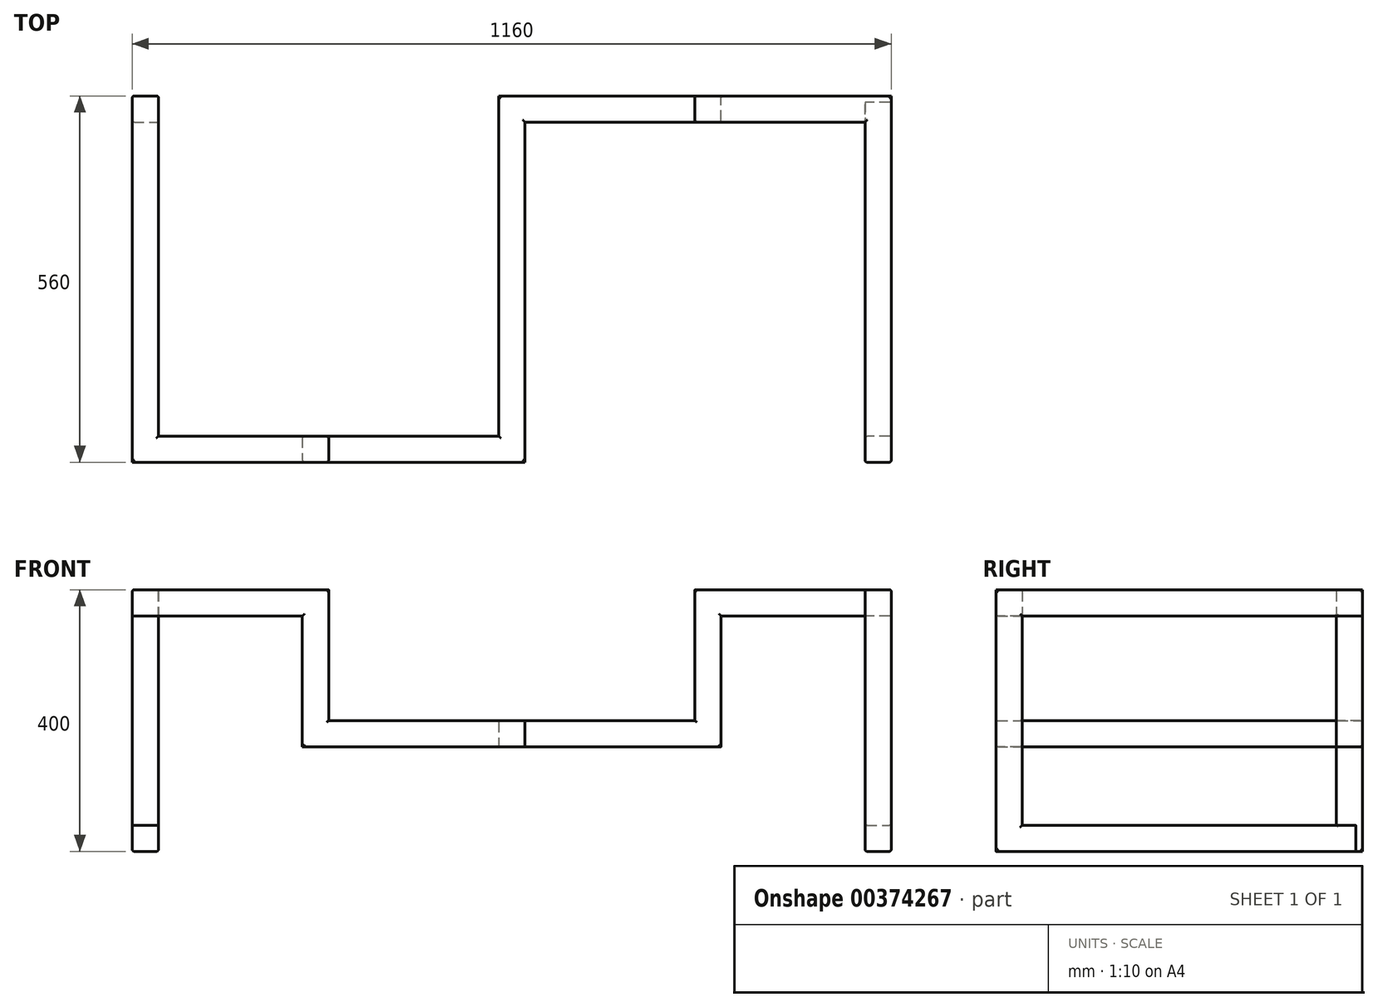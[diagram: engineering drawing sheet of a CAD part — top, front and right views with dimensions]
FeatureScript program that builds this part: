
annotation { "Feature Type Name" : "Feature", "Feature Type Description" : "" }
export const myFeature = defineFeature(function(context is Context, id is Id, definition is map)
    precondition{}
    {
        {
            var Q0;
            Q0=qCreatedBy(makeId("Front.planeOp"),FACE);
            var sketch = newSketch(context, id + "F0", { "sketchPlane" : qUnion([Q0])});
            skLineSegment(sketch, "E0.bottom", {"start": v(0, 0) * mm, "end": v(40, 0) * mm});
            skLineSegment(sketch, "E0.top", {"start": v(0, 40) * mm, "end": v(40, 40) * mm});
            skLineSegment(sketch, "E0.left", {"start": v(0, 0) * mm, "end": v(0, 40) * mm});
            skLineSegment(sketch, "E0.right", {"start": v(40, 0) * mm, "end": v(40, 40) * mm});
            skSolve(sketch);
        }
        {
            var Q0;
            Q0=makeQuery(id+"F0.imprint","IMPRINT",FACE,{"disambiguationData":[TD([[makeQuery(id+"F0.imprint","IMPRINT",EDGE,{"derivedFrom":sQuery(id+"F0.wireOp",EDGE,"E0.bottom")}),1.0]])]});
            extrude(context, id + "F1", {"entities" : qUnion([Q0]), "oppositeDirection" : true, "depth" : 560 * mm});
        }
        {
            var Q0;
            Q0=makeQuery(id+"F1.opExtrude","SWEPT_FACE",FACE,{"disambiguationData":[OSD([sQuery(id+"F0.wireOp",EDGE,"E0.top")])]});
            var sketch = newSketch(context, id + "F2", { "sketchPlane" : qUnion([Q0])});
            skLineSegment(sketch, "E1.bottom", {"start": v(0, 560) * mm, "end": v(40, 560) * mm});
            skLineSegment(sketch, "E1.top", {"start": v(0, 520) * mm, "end": v(40, 520) * mm});
            skLineSegment(sketch, "E1.left", {"start": v(0, 560) * mm, "end": v(0, 520) * mm});
            skLineSegment(sketch, "E1.right", {"start": v(40, 560) * mm, "end": v(40, 520) * mm});
            skSolve(sketch);
        }
        {
            var Q0;
            Q0=makeQuery(id+"F2.imprint","IMPRINT",FACE,{"disambiguationData":[TD([[makeQuery(id+"F2.imprint","IMPRINT",EDGE,{"derivedFrom":sQuery(id+"F2.wireOp",EDGE,"E1.bottom")}),-1.0]])]});
            extrude(context, id + "F3", {"entities" : qUnion([Q0]), "operationType" : NewBodyOperationType.ADD, "depth" : 360 * mm});
        }
        {
            var Q0;
            Q0=makeQuery(id+"F3.opExtrude","SWEPT_FACE",FACE,{"disambiguationData":[OSD([sQuery(id+"F2.wireOp",EDGE,"E1.top")])]});
            var sketch = newSketch(context, id + "F4", { "sketchPlane" : qUnion([Q0])});
            skLineSegment(sketch, "E2.bottom", {"start": v(0, 400) * mm, "end": v(40, 400) * mm});
            skLineSegment(sketch, "E2.top", {"start": v(0, 360) * mm, "end": v(40, 360) * mm});
            skLineSegment(sketch, "E2.left", {"start": v(0, 400) * mm, "end": v(0, 360) * mm});
            skLineSegment(sketch, "E2.right", {"start": v(40, 400) * mm, "end": v(40, 360) * mm});
            skSolve(sketch);
        }
        {
            var Q0;
            Q0=makeQuery(id+"F4.imprint","IMPRINT",FACE,{"disambiguationData":[TD([[makeQuery(id+"F4.imprint","IMPRINT",EDGE,{"derivedFrom":sQuery(id+"F4.wireOp",EDGE,"E2.bottom")}),-1.0]])]});
            extrude(context, id + "F5", {"entities" : qUnion([Q0]), "operationType" : NewBodyOperationType.ADD, "depth" : 520 * mm});
        }
        {
            var Q0;
            Q0=makeQuery(id+"F5.boolean.opBoolean","MERGE",FACE,{"derivedFrom":[makeQuery(id+"F3.boolean.opBoolean","MERGE",FACE,{"derivedFrom":[makeQuery(id+"F1.opExtrude","SWEPT_FACE",FACE,{"disambiguationData":[OSD([sQuery(id+"F0.wireOp",EDGE,"E0.right")])]}),makeQuery(id+"F3.opExtrude","SWEPT_FACE",FACE,{"disambiguationData":[OSD([sQuery(id+"F2.wireOp",EDGE,"E1.right")])]})]}),makeQuery(id+"F5.opExtrude","SWEPT_FACE",FACE,{"disambiguationData":[OSD([sQuery(id+"F4.wireOp",EDGE,"E2.right")])]})]});
            var sketch = newSketch(context, id + "F6", { "sketchPlane" : qUnion([Q0])});
            skLineSegment(sketch, "E3.bottom", {"start": v(0, 400) * mm, "end": v(40, 400) * mm});
            skLineSegment(sketch, "E3.top", {"start": v(0, 360) * mm, "end": v(40, 360) * mm});
            skLineSegment(sketch, "E3.left", {"start": v(0, 400) * mm, "end": v(0, 360) * mm});
            skLineSegment(sketch, "E3.right", {"start": v(40, 400) * mm, "end": v(40, 360) * mm});
            skSolve(sketch);
        }
        {
            var Q0;
            Q0 = qSketchRegion(id + "F6", true);
            extrude(context, id + "F7", {"entities" : qUnion([Q0]), "operationType" : NewBodyOperationType.ADD, "depth" : 260 * mm});
        }
        {
            var Q0;
            Q0=makeQuery(id+"F7.boolean.opBoolean","MERGE",FACE,{"derivedFrom":[makeQuery(id+"F5.opExtrude","SWEPT_FACE",FACE,{"disambiguationData":[OSD([sQuery(id+"F4.wireOp",EDGE,"E2.top")])]}),makeQuery(id+"F7.opExtrude","SWEPT_FACE",FACE,{"disambiguationData":[OSD([sQuery(id+"F6.wireOp",EDGE,"E3.top")])]})]});
            var sketch = newSketch(context, id + "F8", { "sketchPlane" : qUnion([Q0])});
            skLineSegment(sketch, "E4.bottom", {"start": v(300, -40) * mm, "end": v(260, -40) * mm});
            skLineSegment(sketch, "E4.top", {"start": v(300, 0) * mm, "end": v(260, 0) * mm});
            skLineSegment(sketch, "E4.left", {"start": v(300, -40) * mm, "end": v(300, 0) * mm});
            skLineSegment(sketch, "E4.right", {"start": v(260, -40) * mm, "end": v(260, 0) * mm});
            skSolve(sketch);
        }
        {
            var Q0;
            Q0 = qSketchRegion(id + "F8", true);
            extrude(context, id + "F9", {"entities" : qUnion([Q0]), "operationType" : NewBodyOperationType.ADD, "depth" : 200 * mm});
        }
        {
            var Q0;
            Q0=makeQuery(id+"F9.boolean.opBoolean","MERGE",FACE,{"derivedFrom":[makeQuery(id+"F7.opExtrude","CAP_FACE",FACE,{"disambiguationData":[OSD([sQuery(id+"F6.wireOp",EDGE,"E3.bottom"),sQuery(id+"F6.wireOp",EDGE,"E3.top"),sQuery(id+"F6.wireOp",EDGE,"E3.left"),sQuery(id+"F6.wireOp",EDGE,"E3.right")])],"isStart":false}),makeQuery(id+"F9.opExtrude","SWEPT_FACE",FACE,{"disambiguationData":[OSD([sQuery(id+"F8.wireOp",EDGE,"E4.left")])]})]});
            var sketch = newSketch(context, id + "F10", { "sketchPlane" : qUnion([Q0])});
            skLineSegment(sketch, "E5.bottom", {"start": v(0, 160) * mm, "end": v(40, 160) * mm});
            skLineSegment(sketch, "E5.top", {"start": v(0, 200) * mm, "end": v(40, 200) * mm});
            skLineSegment(sketch, "E5.left", {"start": v(0, 160) * mm, "end": v(0, 200) * mm});
            skLineSegment(sketch, "E5.right", {"start": v(40, 160) * mm, "end": v(40, 200) * mm});
            skSolve(sketch);
        }
        {
            var Q0;
            Q0 = qSketchRegion(id + "F10", true);
            extrude(context, id + "F11", {"entities" : qUnion([Q0]), "operationType" : NewBodyOperationType.ADD, "depth" : 300 * mm});
        }
        {
            var Q0;
            Q0=makeQuery(id+"F11.boolean.opBoolean","MERGE",FACE,{"derivedFrom":[makeQuery(id+"F9.boolean.opBoolean","MERGE",FACE,{"derivedFrom":[makeQuery(id+"F7.opExtrude","SWEPT_FACE",FACE,{"disambiguationData":[OSD([sQuery(id+"F6.wireOp",EDGE,"E3.right")])]}),makeQuery(id+"F9.opExtrude","SWEPT_FACE",FACE,{"disambiguationData":[OSD([sQuery(id+"F8.wireOp",EDGE,"E4.bottom")])]})]}),makeQuery(id+"F11.opExtrude","SWEPT_FACE",FACE,{"disambiguationData":[OSD([sQuery(id+"F10.wireOp",EDGE,"E5.right")])]})]});
            var sketch = newSketch(context, id + "F12", { "sketchPlane" : qUnion([Q0])});
            skLineSegment(sketch, "E6.bottom", {"start": v(-600, 200) * mm, "end": v(-560, 200) * mm});
            skLineSegment(sketch, "E6.top", {"start": v(-600, 160) * mm, "end": v(-560, 160) * mm});
            skLineSegment(sketch, "E6.left", {"start": v(-600, 200) * mm, "end": v(-600, 160) * mm});
            skLineSegment(sketch, "E6.right", {"start": v(-560, 200) * mm, "end": v(-560, 160) * mm});
            skSolve(sketch);
        }
        {
            var Q0;
            Q0 = qSketchRegion(id + "F12", true);
            extrude(context, id + "F13", {"entities" : qUnion([Q0]), "operationType" : NewBodyOperationType.ADD, "depth" : 520 * mm});
        }
        {
            var Q0;
            Q0=makeQuery(id+"F13.boolean.opBoolean","MERGE",FACE,{"derivedFrom":[makeQuery(id+"F11.opExtrude","CAP_FACE",FACE,{"disambiguationData":[OSD([sQuery(id+"F10.wireOp",EDGE,"E5.bottom"),sQuery(id+"F10.wireOp",EDGE,"E5.top"),sQuery(id+"F10.wireOp",EDGE,"E5.left"),sQuery(id+"F10.wireOp",EDGE,"E5.right")])],"isStart":false}),makeQuery(id+"F13.opExtrude","SWEPT_FACE",FACE,{"disambiguationData":[OSD([sQuery(id+"F12.wireOp",EDGE,"E6.left")])]})]});
            var sketch = newSketch(context, id + "F14", { "sketchPlane" : qUnion([Q0])});
            skLineSegment(sketch, "E7.bottom", {"start": v(560, 200) * mm, "end": v(520, 200) * mm});
            skLineSegment(sketch, "E7.top", {"start": v(560, 160) * mm, "end": v(520, 160) * mm});
            skLineSegment(sketch, "E7.left", {"start": v(560, 200) * mm, "end": v(560, 160) * mm});
            skLineSegment(sketch, "E7.right", {"start": v(520, 200) * mm, "end": v(520, 160) * mm});
            skSolve(sketch);
        }
        {
            var Q0;
            Q0 = qSketchRegion(id + "F14", true);
            extrude(context, id + "F15", {"entities" : qUnion([Q0]), "operationType" : NewBodyOperationType.ADD, "depth" : 300 * mm});
        }
        {
            var Q0;
            Q0=makeQuery(id+"F15.boolean.opBoolean","MERGE",FACE,{"derivedFrom":[makeQuery(id+"F13.boolean.opBoolean","MERGE",FACE,{"derivedFrom":[makeQuery(id+"F11.opExtrude","SWEPT_FACE",FACE,{"disambiguationData":[OSD([sQuery(id+"F10.wireOp",EDGE,"E5.top")])]}),makeQuery(id+"F13.opExtrude","SWEPT_FACE",FACE,{"disambiguationData":[OSD([sQuery(id+"F12.wireOp",EDGE,"E6.bottom")])]})]}),makeQuery(id+"F15.opExtrude","SWEPT_FACE",FACE,{"disambiguationData":[OSD([sQuery(id+"F14.wireOp",EDGE,"E7.bottom")])]})]});
            var sketch = newSketch(context, id + "F16", { "sketchPlane" : qUnion([Q0])});
            skLineSegment(sketch, "E8.bottom", {"start": v(900, 520) * mm, "end": v(860, 520) * mm});
            skLineSegment(sketch, "E8.top", {"start": v(900, 560) * mm, "end": v(860, 560) * mm});
            skLineSegment(sketch, "E8.left", {"start": v(900, 520) * mm, "end": v(900, 560) * mm});
            skLineSegment(sketch, "E8.right", {"start": v(860, 520) * mm, "end": v(860, 560) * mm});
            skSolve(sketch);
        }
        {
            var Q0;
            Q0 = qSketchRegion(id + "F16", true);
            extrude(context, id + "F17", {"entities" : qUnion([Q0]), "operationType" : NewBodyOperationType.ADD, "depth" : 200 * mm});
        }
        {
            var Q0;
            Q0=makeQuery(id+"F17.boolean.opBoolean","MERGE",FACE,{"derivedFrom":[makeQuery(id+"F15.opExtrude","CAP_FACE",FACE,{"disambiguationData":[OSD([sQuery(id+"F14.wireOp",EDGE,"E7.bottom"),sQuery(id+"F14.wireOp",EDGE,"E7.top"),sQuery(id+"F14.wireOp",EDGE,"E7.left"),sQuery(id+"F14.wireOp",EDGE,"E7.right")])],"isStart":false}),makeQuery(id+"F17.opExtrude","SWEPT_FACE",FACE,{"disambiguationData":[OSD([sQuery(id+"F16.wireOp",EDGE,"E8.left")])]})]});
            var sketch = newSketch(context, id + "F18", { "sketchPlane" : qUnion([Q0])});
            skLineSegment(sketch, "E9.bottom", {"start": v(520, 400) * mm, "end": v(560, 400) * mm});
            skLineSegment(sketch, "E9.top", {"start": v(520, 360) * mm, "end": v(560, 360) * mm});
            skLineSegment(sketch, "E9.left", {"start": v(520, 400) * mm, "end": v(520, 360) * mm});
            skLineSegment(sketch, "E9.right", {"start": v(560, 400) * mm, "end": v(560, 360) * mm});
            skSolve(sketch);
        }
        {
            var Q0;
            Q0 = qSketchRegion(id + "F18", true);
            extrude(context, id + "F19", {"entities" : qUnion([Q0]), "operationType" : NewBodyOperationType.ADD, "depth" : 260 * mm});
        }
        {
            var Q0;
            Q0=makeQuery(id+"F19.boolean.opBoolean","MERGE",FACE,{"derivedFrom":[makeQuery(id+"F17.boolean.opBoolean","MERGE",FACE,{"derivedFrom":[makeQuery(id+"F15.opExtrude","SWEPT_FACE",FACE,{"disambiguationData":[OSD([sQuery(id+"F14.wireOp",EDGE,"E7.right")])]}),makeQuery(id+"F17.opExtrude","SWEPT_FACE",FACE,{"disambiguationData":[OSD([sQuery(id+"F16.wireOp",EDGE,"E8.bottom")])]})]}),makeQuery(id+"F19.opExtrude","SWEPT_FACE",FACE,{"disambiguationData":[OSD([sQuery(id+"F18.wireOp",EDGE,"E9.left")])]})]});
            var sketch = newSketch(context, id + "F20", { "sketchPlane" : qUnion([Q0])});
            skLineSegment(sketch, "E10.bottom", {"start": v(1160, 400) * mm, "end": v(1120, 400) * mm});
            skLineSegment(sketch, "E10.top", {"start": v(1160, 360) * mm, "end": v(1120, 360) * mm});
            skLineSegment(sketch, "E10.left", {"start": v(1160, 400) * mm, "end": v(1160, 360) * mm});
            skLineSegment(sketch, "E10.right", {"start": v(1120, 400) * mm, "end": v(1120, 360) * mm});
            skSolve(sketch);
        }
        {
            var Q0;
            Q0 = qSketchRegion(id + "F20", true);
            extrude(context, id + "F21", {"entities" : qUnion([Q0]), "operationType" : NewBodyOperationType.ADD, "depth" : 520 * mm});
        }
        {
            var Q0;
            Q0=makeQuery(id+"F21.boolean.opBoolean","MERGE",FACE,{"derivedFrom":[makeQuery(id+"F19.opExtrude","SWEPT_FACE",FACE,{"disambiguationData":[OSD([sQuery(id+"F18.wireOp",EDGE,"E9.top")])]}),makeQuery(id+"F21.opExtrude","SWEPT_FACE",FACE,{"disambiguationData":[OSD([sQuery(id+"F20.wireOp",EDGE,"E10.top")])]})]});
            var sketch = newSketch(context, id + "F22", { "sketchPlane" : qUnion([Q0])});
            skLineSegment(sketch, "E11.bottom", {"start": v(1160, 0) * mm, "end": v(1120, 0) * mm});
            skLineSegment(sketch, "E11.top", {"start": v(1160, -40) * mm, "end": v(1120, -40) * mm});
            skLineSegment(sketch, "E11.left", {"start": v(1160, 0) * mm, "end": v(1160, -40) * mm});
            skLineSegment(sketch, "E11.right", {"start": v(1120, 0) * mm, "end": v(1120, -40) * mm});
            skSolve(sketch);
        }
        {
            var Q0;
            Q0 = qSketchRegion(id + "F22", true);
            extrude(context, id + "F23", {"entities" : qUnion([Q0]), "operationType" : NewBodyOperationType.ADD, "depth" : 360 * mm});
        }
        {
            var Q0;
            Q0=makeQuery(id+"F23.opExtrude","SWEPT_FACE",FACE,{"disambiguationData":[OSD([sQuery(id+"F22.wireOp",EDGE,"E11.top")])]});
            var sketch = newSketch(context, id + "F24", { "sketchPlane" : qUnion([Q0])});
            skLineSegment(sketch, "E12.bottom", {"start": v(-1120, 0) * mm, "end": v(-1160, 0) * mm});
            skLineSegment(sketch, "E12.top", {"start": v(-1120, 40) * mm, "end": v(-1160, 40) * mm});
            skLineSegment(sketch, "E12.left", {"start": v(-1120, 0) * mm, "end": v(-1120, 40) * mm});
            skLineSegment(sketch, "E12.right", {"start": v(-1160, 0) * mm, "end": v(-1160, 40) * mm});
            skSolve(sketch);
        }
        {
            var Q0;
            Q0 = qSketchRegion(id + "F24", true);
            extrude(context, id + "F25", {"entities" : qUnion([Q0]), "operationType" : NewBodyOperationType.ADD, "depth" : 510 * mm});
        }
        {
            var Q0;
            Q0=makeQuery(id+"F5.boolean.opBoolean","MERGE",EDGE,{"derivedFrom":[makeQuery(id+"F3.opExtrude","CAP_EDGE",EDGE,{"disambiguationData":[OSD([sQuery(id+"F2.wireOp",EDGE,"E1.left")])],"isStart":false}),makeQuery(id+"F5.opExtrude","SWEPT_EDGE",EDGE,{"disambiguationData":[OSD([sQuery(id+"F4.wireOp",EDGE,"E2.bottom"),sQuery(id+"F4.wireOp",EDGE,"E2.left")])]})]});
            var Q1;
            Q1=makeQuery(id+"F7.boolean.opBoolean","MERGE",EDGE,{"derivedFrom":[makeQuery(id+"F5.opExtrude","CAP_EDGE",EDGE,{"disambiguationData":[OSD([sQuery(id+"F4.wireOp",EDGE,"E2.bottom")])],"isStart":false}),makeQuery(id+"F7.opExtrude","SWEPT_EDGE",EDGE,{"disambiguationData":[OSD([sQuery(id+"F6.wireOp",EDGE,"E3.bottom"),sQuery(id+"F6.wireOp",EDGE,"E3.left")])]})]});
            var Q2;
            Q2=makeQuery(id+"F7.opExtrude","SWEPT_EDGE",EDGE,{"disambiguationData":[OSD([sQuery(id+"F2.wireOp",EDGE,"E1.right"),sQuery(id+"F4.wireOp",EDGE,"E2.bottom"),sQuery(id+"F4.wireOp",EDGE,"E2.right"),sQuery(id+"F6.wireOp",EDGE,"E3.bottom"),sQuery(id+"F6.wireOp",EDGE,"E3.right")])]});
            var Q3;
            Q3=makeQuery(id+"F5.boolean.opBoolean","MERGE",EDGE,{"derivedFrom":[makeQuery(id+"F3.opExtrude","CAP_EDGE",EDGE,{"disambiguationData":[OSD([sQuery(id+"F2.wireOp",EDGE,"E1.right")])],"isStart":false}),makeQuery(id+"F5.opExtrude","SWEPT_EDGE",EDGE,{"disambiguationData":[OSD([sQuery(id+"F4.wireOp",EDGE,"E2.bottom"),sQuery(id+"F4.wireOp",EDGE,"E2.right")])]})]});
            var Q4;
            Q4=makeQuery(id+"F5.opExtrude","SWEPT_EDGE",EDGE,{"disambiguationData":[OSD([sQuery(id+"F0.wireOp",EDGE,"E0.top"),sQuery(id+"F0.wireOp",EDGE,"E0.left"),sQuery(id+"F2.wireOp",EDGE,"E1.top"),sQuery(id+"F2.wireOp",EDGE,"E1.left"),sQuery(id+"F4.wireOp",EDGE,"E2.top"),sQuery(id+"F4.wireOp",EDGE,"E2.left")])]});
            var Q5;
            Q5=makeQuery(id+"F7.boolean.opBoolean","MERGE",EDGE,{"derivedFrom":[makeQuery(id+"F5.opExtrude","CAP_EDGE",EDGE,{"disambiguationData":[OSD([sQuery(id+"F4.wireOp",EDGE,"E2.top")])],"isStart":false}),makeQuery(id+"F7.opExtrude","SWEPT_EDGE",EDGE,{"disambiguationData":[OSD([sQuery(id+"F6.wireOp",EDGE,"E3.top"),sQuery(id+"F6.wireOp",EDGE,"E3.left")])]})]});
            var Q6;
            Q6=makeQuery(id+"F9.opExtrude","SWEPT_EDGE",EDGE,{"disambiguationData":[OSD([sQuery(id+"F4.wireOp",EDGE,"E2.top"),sQuery(id+"F6.wireOp",EDGE,"E3.top"),sQuery(id+"F6.wireOp",EDGE,"E3.left"),sQuery(id+"F8.wireOp",EDGE,"E4.top"),sQuery(id+"F8.wireOp",EDGE,"E4.right")])]});
            var Q7;
            Q7=makeQuery(id+"F9.opExtrude","SWEPT_EDGE",EDGE,{"disambiguationData":[OSD([sQuery(id+"F0.wireOp",EDGE,"E0.top"),sQuery(id+"F0.wireOp",EDGE,"E0.right"),sQuery(id+"F2.wireOp",EDGE,"E1.top"),sQuery(id+"F2.wireOp",EDGE,"E1.right"),sQuery(id+"F4.wireOp",EDGE,"E2.top"),sQuery(id+"F4.wireOp",EDGE,"E2.right"),sQuery(id+"F6.wireOp",EDGE,"E3.top"),sQuery(id+"F6.wireOp",EDGE,"E3.right"),sQuery(id+"F8.wireOp",EDGE,"E4.bottom"),sQuery(id+"F8.wireOp",EDGE,"E4.right")])]});
            var Q8;
            Q8=makeQuery(id+"F9.boolean.opBoolean","MERGE",EDGE,{"derivedFrom":[makeQuery(id+"F7.opExtrude","CAP_EDGE",EDGE,{"disambiguationData":[OSD([sQuery(id+"F6.wireOp",EDGE,"E3.left")])],"isStart":false}),makeQuery(id+"F9.opExtrude","SWEPT_EDGE",EDGE,{"disambiguationData":[OSD([sQuery(id+"F8.wireOp",EDGE,"E4.top"),sQuery(id+"F8.wireOp",EDGE,"E4.left")])]})]});
            var Q9;
            Q9=makeQuery(id+"F11.opExtrude","SWEPT_EDGE",EDGE,{"disambiguationData":[OSD([sQuery(id+"F6.wireOp",EDGE,"E3.right"),sQuery(id+"F8.wireOp",EDGE,"E4.bottom"),sQuery(id+"F8.wireOp",EDGE,"E4.left"),sQuery(id+"F10.wireOp",EDGE,"E5.top"),sQuery(id+"F10.wireOp",EDGE,"E5.right")])]});
            var Q10;
            Q10=makeQuery(id+"F11.opExtrude","SWEPT_EDGE",EDGE,{"disambiguationData":[OSD([sQuery(id+"F6.wireOp",EDGE,"E3.left"),sQuery(id+"F8.wireOp",EDGE,"E4.top"),sQuery(id+"F8.wireOp",EDGE,"E4.left"),sQuery(id+"F10.wireOp",EDGE,"E5.top"),sQuery(id+"F10.wireOp",EDGE,"E5.left")])]});
            var Q11;
            Q11=makeQuery(id+"F11.boolean.opBoolean","MERGE",EDGE,{"derivedFrom":[makeQuery(id+"F9.opExtrude","CAP_EDGE",EDGE,{"disambiguationData":[OSD([sQuery(id+"F8.wireOp",EDGE,"E4.top")])],"isStart":false}),makeQuery(id+"F11.opExtrude","SWEPT_EDGE",EDGE,{"disambiguationData":[OSD([sQuery(id+"F10.wireOp",EDGE,"E5.bottom"),sQuery(id+"F10.wireOp",EDGE,"E5.left")])]})]});
            var Q12;
            Q12=makeQuery(id+"F3.opExtrude","SWEPT_EDGE",EDGE,{"disambiguationData":[OSD([sQuery(id+"F0.wireOp",EDGE,"E0.top"),sQuery(id+"F0.wireOp",EDGE,"E0.right"),sQuery(id+"F2.wireOp",EDGE,"E1.top"),sQuery(id+"F2.wireOp",EDGE,"E1.right")])]});
            var Q13;
            Q13=makeQuery(id+"F3.opExtrude","SWEPT_EDGE",EDGE,{"disambiguationData":[OSD([sQuery(id+"F0.wireOp",EDGE,"E0.top"),sQuery(id+"F0.wireOp",EDGE,"E0.left"),sQuery(id+"F2.wireOp",EDGE,"E1.top"),sQuery(id+"F2.wireOp",EDGE,"E1.left")])]});
            var Q14;
            Q14=makeQuery(id+"F3.boolean.opBoolean","MERGE",EDGE,{"derivedFrom":[makeQuery(id+"F1.opExtrude","CAP_EDGE",EDGE,{"disambiguationData":[OSD([sQuery(id+"F0.wireOp",EDGE,"E0.left")])],"isStart":false}),makeQuery(id+"F3.opExtrude","SWEPT_EDGE",EDGE,{"disambiguationData":[OSD([sQuery(id+"F2.wireOp",EDGE,"E1.bottom"),sQuery(id+"F2.wireOp",EDGE,"E1.left")])]})]});
            var Q15;
            Q15=makeQuery(id+"F1.opExtrude","SWEPT_EDGE",EDGE,{"disambiguationData":[OSD([sQuery(id+"F0.wireOp",EDGE,"E0.top"),sQuery(id+"F0.wireOp",EDGE,"E0.left")])]});
            var Q16;
            Q16=makeQuery(id+"F1.opExtrude","SWEPT_EDGE",EDGE,{"disambiguationData":[OSD([sQuery(id+"F0.wireOp",EDGE,"E0.bottom"),sQuery(id+"F0.wireOp",EDGE,"E0.left")])]});
            var Q17;
            Q17=makeQuery(id+"F1.opExtrude","SWEPT_EDGE",EDGE,{"disambiguationData":[OSD([sQuery(id+"F0.wireOp",EDGE,"E0.top"),sQuery(id+"F0.wireOp",EDGE,"E0.right")])]});
            var Q18;
            Q18=makeQuery(id+"F13.opExtrude","SWEPT_EDGE",EDGE,{"disambiguationData":[OSD([sQuery(id+"F6.wireOp",EDGE,"E3.right"),sQuery(id+"F8.wireOp",EDGE,"E4.bottom"),sQuery(id+"F8.wireOp",EDGE,"E4.left"),sQuery(id+"F10.wireOp",EDGE,"E5.top"),sQuery(id+"F10.wireOp",EDGE,"E5.right"),sQuery(id+"F12.wireOp",EDGE,"E6.bottom"),sQuery(id+"F12.wireOp",EDGE,"E6.right")])]});
            var Q19;
            Q19=makeQuery(id+"F13.boolean.opBoolean","MERGE",EDGE,{"derivedFrom":[makeQuery(id+"F11.opExtrude","CAP_EDGE",EDGE,{"disambiguationData":[OSD([sQuery(id+"F10.wireOp",EDGE,"E5.top")])],"isStart":false}),makeQuery(id+"F13.opExtrude","SWEPT_EDGE",EDGE,{"disambiguationData":[OSD([sQuery(id+"F12.wireOp",EDGE,"E6.bottom"),sQuery(id+"F12.wireOp",EDGE,"E6.left")])]})]});
            var Q20;
            Q20=makeQuery(id+"F15.boolean.opBoolean","MERGE",EDGE,{"derivedFrom":[makeQuery(id+"F13.opExtrude","CAP_EDGE",EDGE,{"disambiguationData":[OSD([sQuery(id+"F12.wireOp",EDGE,"E6.bottom")])],"isStart":false}),makeQuery(id+"F15.opExtrude","SWEPT_EDGE",EDGE,{"disambiguationData":[OSD([sQuery(id+"F14.wireOp",EDGE,"E7.bottom"),sQuery(id+"F14.wireOp",EDGE,"E7.left")])]})]});
            var Q21;
            Q21=makeQuery(id+"F15.opExtrude","SWEPT_EDGE",EDGE,{"disambiguationData":[OSD([sQuery(id+"F10.wireOp",EDGE,"E5.top"),sQuery(id+"F12.wireOp",EDGE,"E6.bottom"),sQuery(id+"F12.wireOp",EDGE,"E6.left"),sQuery(id+"F14.wireOp",EDGE,"E7.bottom"),sQuery(id+"F14.wireOp",EDGE,"E7.right")])]});
            var Q22;
            Q22=makeQuery(id+"F15.opExtrude","SWEPT_EDGE",EDGE,{"disambiguationData":[OSD([sQuery(id+"F10.wireOp",EDGE,"E5.bottom"),sQuery(id+"F12.wireOp",EDGE,"E6.top"),sQuery(id+"F12.wireOp",EDGE,"E6.left"),sQuery(id+"F14.wireOp",EDGE,"E7.top"),sQuery(id+"F14.wireOp",EDGE,"E7.right")])]});
            var Q23;
            Q23=makeQuery(id+"F13.opExtrude","SWEPT_EDGE",EDGE,{"disambiguationData":[OSD([sQuery(id+"F8.wireOp",EDGE,"E4.bottom"),sQuery(id+"F10.wireOp",EDGE,"E5.bottom"),sQuery(id+"F10.wireOp",EDGE,"E5.right"),sQuery(id+"F12.wireOp",EDGE,"E6.top"),sQuery(id+"F12.wireOp",EDGE,"E6.right")])]});
            var Q24;
            Q24=makeQuery(id+"F25.boolean.opBoolean","MERGE",EDGE,{"derivedFrom":[makeQuery(id+"F23.opExtrude","CAP_EDGE",EDGE,{"disambiguationData":[OSD([sQuery(id+"F22.wireOp",EDGE,"E11.right")])],"isStart":false}),makeQuery(id+"F25.opExtrude","SWEPT_EDGE",EDGE,{"disambiguationData":[OSD([sQuery(id+"F24.wireOp",EDGE,"E12.bottom"),sQuery(id+"F24.wireOp",EDGE,"E12.left")])]})]});
            var Q25;
            Q25=makeQuery(id+"F25.opExtrude","SWEPT_EDGE",EDGE,{"disambiguationData":[OSD([sQuery(id+"F18.wireOp",EDGE,"E9.top"),sQuery(id+"F20.wireOp",EDGE,"E10.top"),sQuery(id+"F20.wireOp",EDGE,"E10.left"),sQuery(id+"F22.wireOp",EDGE,"E11.top"),sQuery(id+"F22.wireOp",EDGE,"E11.left"),sQuery(id+"F24.wireOp",EDGE,"E12.top"),sQuery(id+"F24.wireOp",EDGE,"E12.right")])]});
            var Q26;
            Q26=makeQuery(id+"F25.opExtrude","SWEPT_EDGE",EDGE,{"disambiguationData":[OSD([sQuery(id+"F14.wireOp",EDGE,"E7.right"),sQuery(id+"F16.wireOp",EDGE,"E8.bottom"),sQuery(id+"F16.wireOp",EDGE,"E8.left"),sQuery(id+"F18.wireOp",EDGE,"E9.top"),sQuery(id+"F18.wireOp",EDGE,"E9.left"),sQuery(id+"F20.wireOp",EDGE,"E10.top"),sQuery(id+"F20.wireOp",EDGE,"E10.right"),sQuery(id+"F22.wireOp",EDGE,"E11.top"),sQuery(id+"F22.wireOp",EDGE,"E11.right"),sQuery(id+"F24.wireOp",EDGE,"E12.top"),sQuery(id+"F24.wireOp",EDGE,"E12.left")])]});
            var Q27;
            Q27=makeQuery(id+"F23.opExtrude","SWEPT_EDGE",EDGE,{"disambiguationData":[OSD([sQuery(id+"F14.wireOp",EDGE,"E7.right"),sQuery(id+"F16.wireOp",EDGE,"E8.bottom"),sQuery(id+"F16.wireOp",EDGE,"E8.left"),sQuery(id+"F18.wireOp",EDGE,"E9.top"),sQuery(id+"F18.wireOp",EDGE,"E9.left"),sQuery(id+"F20.wireOp",EDGE,"E10.top"),sQuery(id+"F20.wireOp",EDGE,"E10.right"),sQuery(id+"F22.wireOp",EDGE,"E11.top"),sQuery(id+"F22.wireOp",EDGE,"E11.right")])]});
            var Q28;
            Q28=makeQuery(id+"F23.boolean.opBoolean","MERGE",EDGE,{"derivedFrom":[makeQuery(id+"F21.opExtrude","CAP_EDGE",EDGE,{"disambiguationData":[OSD([sQuery(id+"F20.wireOp",EDGE,"E10.left")])],"isStart":false}),makeQuery(id+"F23.opExtrude","SWEPT_EDGE",EDGE,{"disambiguationData":[OSD([sQuery(id+"F22.wireOp",EDGE,"E11.bottom"),sQuery(id+"F22.wireOp",EDGE,"E11.left")])]})]});
            var Q29;
            Q29=makeQuery(id+"F23.boolean.opBoolean","MERGE",EDGE,{"derivedFrom":[makeQuery(id+"F21.opExtrude","CAP_EDGE",EDGE,{"disambiguationData":[OSD([sQuery(id+"F20.wireOp",EDGE,"E10.right")])],"isStart":false}),makeQuery(id+"F23.opExtrude","SWEPT_EDGE",EDGE,{"disambiguationData":[OSD([sQuery(id+"F22.wireOp",EDGE,"E11.bottom"),sQuery(id+"F22.wireOp",EDGE,"E11.right")])]})]});
            var Q30;
            Q30=makeQuery(id+"F21.opExtrude","SWEPT_EDGE",EDGE,{"disambiguationData":[OSD([sQuery(id+"F14.wireOp",EDGE,"E7.right"),sQuery(id+"F16.wireOp",EDGE,"E8.bottom"),sQuery(id+"F16.wireOp",EDGE,"E8.left"),sQuery(id+"F18.wireOp",EDGE,"E9.top"),sQuery(id+"F18.wireOp",EDGE,"E9.left"),sQuery(id+"F20.wireOp",EDGE,"E10.top"),sQuery(id+"F20.wireOp",EDGE,"E10.right")])]});
            var Q31;
            Q31=makeQuery(id+"F21.boolean.opBoolean","MERGE",EDGE,{"derivedFrom":[makeQuery(id+"F19.opExtrude","CAP_EDGE",EDGE,{"disambiguationData":[OSD([sQuery(id+"F18.wireOp",EDGE,"E9.bottom")])],"isStart":false}),makeQuery(id+"F21.opExtrude","SWEPT_EDGE",EDGE,{"disambiguationData":[OSD([sQuery(id+"F20.wireOp",EDGE,"E10.bottom"),sQuery(id+"F20.wireOp",EDGE,"E10.left")])]})]});
            var Q32;
            Q32=makeQuery(id+"F21.opExtrude","SWEPT_EDGE",EDGE,{"disambiguationData":[OSD([sQuery(id+"F16.wireOp",EDGE,"E8.bottom"),sQuery(id+"F18.wireOp",EDGE,"E9.bottom"),sQuery(id+"F18.wireOp",EDGE,"E9.left"),sQuery(id+"F20.wireOp",EDGE,"E10.bottom"),sQuery(id+"F20.wireOp",EDGE,"E10.right")])]});
            var Q33;
            Q33=makeQuery(id+"F19.boolean.opBoolean","MERGE",EDGE,{"derivedFrom":[makeQuery(id+"F17.opExtrude","CAP_EDGE",EDGE,{"disambiguationData":[OSD([sQuery(id+"F16.wireOp",EDGE,"E8.top")])],"isStart":false}),makeQuery(id+"F19.opExtrude","SWEPT_EDGE",EDGE,{"disambiguationData":[OSD([sQuery(id+"F18.wireOp",EDGE,"E9.bottom"),sQuery(id+"F18.wireOp",EDGE,"E9.right")])]})]});
            var Q34;
            Q34=makeQuery(id+"F19.boolean.opBoolean","MERGE",EDGE,{"derivedFrom":[makeQuery(id+"F17.opExtrude","CAP_EDGE",EDGE,{"disambiguationData":[OSD([sQuery(id+"F16.wireOp",EDGE,"E8.bottom")])],"isStart":false}),makeQuery(id+"F19.opExtrude","SWEPT_EDGE",EDGE,{"disambiguationData":[OSD([sQuery(id+"F18.wireOp",EDGE,"E9.bottom"),sQuery(id+"F18.wireOp",EDGE,"E9.left")])]})]});
            var Q35;
            Q35=makeQuery(id+"F19.opExtrude","SWEPT_EDGE",EDGE,{"disambiguationData":[OSD([sQuery(id+"F14.wireOp",EDGE,"E7.right"),sQuery(id+"F16.wireOp",EDGE,"E8.bottom"),sQuery(id+"F16.wireOp",EDGE,"E8.left"),sQuery(id+"F18.wireOp",EDGE,"E9.top"),sQuery(id+"F18.wireOp",EDGE,"E9.left")])]});
            var Q36;
            Q36=makeQuery(id+"F17.boolean.opBoolean","MERGE",EDGE,{"derivedFrom":[makeQuery(id+"F15.opExtrude","CAP_EDGE",EDGE,{"disambiguationData":[OSD([sQuery(id+"F14.wireOp",EDGE,"E7.right")])],"isStart":false}),makeQuery(id+"F17.opExtrude","SWEPT_EDGE",EDGE,{"disambiguationData":[OSD([sQuery(id+"F16.wireOp",EDGE,"E8.bottom"),sQuery(id+"F16.wireOp",EDGE,"E8.left")])]})]});
            var Q37;
            Q37=makeQuery(id+"F17.opExtrude","SWEPT_EDGE",EDGE,{"disambiguationData":[OSD([sQuery(id+"F10.wireOp",EDGE,"E5.top"),sQuery(id+"F12.wireOp",EDGE,"E6.bottom"),sQuery(id+"F12.wireOp",EDGE,"E6.left"),sQuery(id+"F14.wireOp",EDGE,"E7.bottom"),sQuery(id+"F14.wireOp",EDGE,"E7.right"),sQuery(id+"F16.wireOp",EDGE,"E8.bottom"),sQuery(id+"F16.wireOp",EDGE,"E8.right")])]});
            var Q38;
            Q38=makeQuery(id+"F17.opExtrude","SWEPT_EDGE",EDGE,{"disambiguationData":[OSD([sQuery(id+"F12.wireOp",EDGE,"E6.bottom"),sQuery(id+"F14.wireOp",EDGE,"E7.bottom"),sQuery(id+"F14.wireOp",EDGE,"E7.left"),sQuery(id+"F16.wireOp",EDGE,"E8.top"),sQuery(id+"F16.wireOp",EDGE,"E8.right")])]});
            var Q39;
            Q39=makeQuery(id+"F21.boolean.opBoolean","MERGE",EDGE,{"derivedFrom":[makeQuery(id+"F19.opExtrude","CAP_EDGE",EDGE,{"disambiguationData":[OSD([sQuery(id+"F18.wireOp",EDGE,"E9.top")])],"isStart":false}),makeQuery(id+"F21.opExtrude","SWEPT_EDGE",EDGE,{"disambiguationData":[OSD([sQuery(id+"F20.wireOp",EDGE,"E10.top"),sQuery(id+"F20.wireOp",EDGE,"E10.left")])]})]});
            var Q40;
            Q40=makeQuery(id+"F25.boolean.opBoolean","MERGE",EDGE,{"derivedFrom":[makeQuery(id+"F23.opExtrude","CAP_EDGE",EDGE,{"disambiguationData":[OSD([sQuery(id+"F22.wireOp",EDGE,"E11.left")])],"isStart":false}),makeQuery(id+"F25.opExtrude","SWEPT_EDGE",EDGE,{"disambiguationData":[OSD([sQuery(id+"F24.wireOp",EDGE,"E12.bottom"),sQuery(id+"F24.wireOp",EDGE,"E12.right")])]})]});
            var Q41;
            Q41=makeQuery(id+"F19.opExtrude","SWEPT_EDGE",EDGE,{"disambiguationData":[OSD([sQuery(id+"F14.wireOp",EDGE,"E7.left"),sQuery(id+"F16.wireOp",EDGE,"E8.top"),sQuery(id+"F16.wireOp",EDGE,"E8.left"),sQuery(id+"F18.wireOp",EDGE,"E9.top"),sQuery(id+"F18.wireOp",EDGE,"E9.right")])]});
            var Q42;
            Q42=makeQuery(id+"F15.boolean.opBoolean","MERGE",EDGE,{"derivedFrom":[makeQuery(id+"F13.opExtrude","CAP_EDGE",EDGE,{"disambiguationData":[OSD([sQuery(id+"F12.wireOp",EDGE,"E6.top")])],"isStart":false}),makeQuery(id+"F15.opExtrude","SWEPT_EDGE",EDGE,{"disambiguationData":[OSD([sQuery(id+"F14.wireOp",EDGE,"E7.top"),sQuery(id+"F14.wireOp",EDGE,"E7.left")])]})]});
            var Q43;
            Q43=makeQuery(id+"F17.boolean.opBoolean","MERGE",EDGE,{"derivedFrom":[makeQuery(id+"F15.opExtrude","CAP_EDGE",EDGE,{"disambiguationData":[OSD([sQuery(id+"F14.wireOp",EDGE,"E7.left")])],"isStart":false}),makeQuery(id+"F17.opExtrude","SWEPT_EDGE",EDGE,{"disambiguationData":[OSD([sQuery(id+"F16.wireOp",EDGE,"E8.top"),sQuery(id+"F16.wireOp",EDGE,"E8.left")])]})]});
            var Q44;
            Q44=makeQuery(id+"F13.boolean.opBoolean","MERGE",EDGE,{"derivedFrom":[makeQuery(id+"F11.opExtrude","CAP_EDGE",EDGE,{"disambiguationData":[OSD([sQuery(id+"F10.wireOp",EDGE,"E5.bottom")])],"isStart":false}),makeQuery(id+"F13.opExtrude","SWEPT_EDGE",EDGE,{"disambiguationData":[OSD([sQuery(id+"F12.wireOp",EDGE,"E6.top"),sQuery(id+"F12.wireOp",EDGE,"E6.left")])]})]});
            var Q45;
            Q45=makeQuery(id+"F11.boolean.opBoolean","MERGE",EDGE,{"derivedFrom":[makeQuery(id+"F9.opExtrude","CAP_EDGE",EDGE,{"disambiguationData":[OSD([sQuery(id+"F8.wireOp",EDGE,"E4.bottom")])],"isStart":false}),makeQuery(id+"F11.opExtrude","SWEPT_EDGE",EDGE,{"disambiguationData":[OSD([sQuery(id+"F10.wireOp",EDGE,"E5.bottom"),sQuery(id+"F10.wireOp",EDGE,"E5.right")])]})]});
            var Q46;
            Q46=makeQuery(id+"F7.opExtrude","SWEPT_EDGE",EDGE,{"disambiguationData":[OSD([sQuery(id+"F0.wireOp",EDGE,"E0.top"),sQuery(id+"F0.wireOp",EDGE,"E0.right"),sQuery(id+"F2.wireOp",EDGE,"E1.top"),sQuery(id+"F2.wireOp",EDGE,"E1.right"),sQuery(id+"F4.wireOp",EDGE,"E2.top"),sQuery(id+"F4.wireOp",EDGE,"E2.right"),sQuery(id+"F6.wireOp",EDGE,"E3.top"),sQuery(id+"F6.wireOp",EDGE,"E3.right")])]});
            var Q47;
            Q47=makeQuery(id+"F9.boolean.opBoolean","MERGE",EDGE,{"derivedFrom":[makeQuery(id+"F7.opExtrude","CAP_EDGE",EDGE,{"disambiguationData":[OSD([sQuery(id+"F6.wireOp",EDGE,"E3.right")])],"isStart":false}),makeQuery(id+"F9.opExtrude","SWEPT_EDGE",EDGE,{"disambiguationData":[OSD([sQuery(id+"F8.wireOp",EDGE,"E4.bottom"),sQuery(id+"F8.wireOp",EDGE,"E4.left")])]})]});
            var Q48;
            Q48=makeQuery(id+"F23.opExtrude","SWEPT_EDGE",EDGE,{"disambiguationData":[OSD([sQuery(id+"F18.wireOp",EDGE,"E9.top"),sQuery(id+"F20.wireOp",EDGE,"E10.top"),sQuery(id+"F20.wireOp",EDGE,"E10.left"),sQuery(id+"F22.wireOp",EDGE,"E11.top"),sQuery(id+"F22.wireOp",EDGE,"E11.left")])]});
            var Q49;
            Q49=makeQuery(id+"F3.boolean.opBoolean","MERGE",EDGE,{"derivedFrom":[makeQuery(id+"F1.opExtrude","CAP_EDGE",EDGE,{"disambiguationData":[OSD([sQuery(id+"F0.wireOp",EDGE,"E0.right")])],"isStart":false}),makeQuery(id+"F3.opExtrude","SWEPT_EDGE",EDGE,{"disambiguationData":[OSD([sQuery(id+"F2.wireOp",EDGE,"E1.bottom"),sQuery(id+"F2.wireOp",EDGE,"E1.right")])]})]});
            var Q50;
            Q50=makeQuery(id+"F5.opExtrude","SWEPT_EDGE",EDGE,{"disambiguationData":[OSD([sQuery(id+"F0.wireOp",EDGE,"E0.top"),sQuery(id+"F0.wireOp",EDGE,"E0.right"),sQuery(id+"F2.wireOp",EDGE,"E1.top"),sQuery(id+"F2.wireOp",EDGE,"E1.right"),sQuery(id+"F4.wireOp",EDGE,"E2.top"),sQuery(id+"F4.wireOp",EDGE,"E2.right")])]});
            var Q51;
            Q51=makeQuery(id+"F1.opExtrude","SWEPT_EDGE",EDGE,{"disambiguationData":[OSD([sQuery(id+"F0.wireOp",EDGE,"E0.bottom"),sQuery(id+"F0.wireOp",EDGE,"E0.right")])]});
            fillet(context, id + "F26", {"entities" : qUnion([Q0, Q1, Q2, Q3, Q4, Q5, Q6, Q7, Q8, Q9, Q10, Q11, Q12, Q13, Q14, Q15, Q16, Q17, Q18, Q19, Q20, Q21, Q22, Q23, Q24, Q25, Q26, Q27, Q28, Q29, Q30, Q31, Q32, Q33, Q34, Q35, Q36, Q37, Q38, Q39, Q40, Q41, Q42, Q43, Q44, Q45, Q46, Q47, Q48, Q49, Q50, Q51]), "radius" : 3 * mm, "tangentPropagation" : true, "allowEdgeOverflow" : false});
        }
    });
